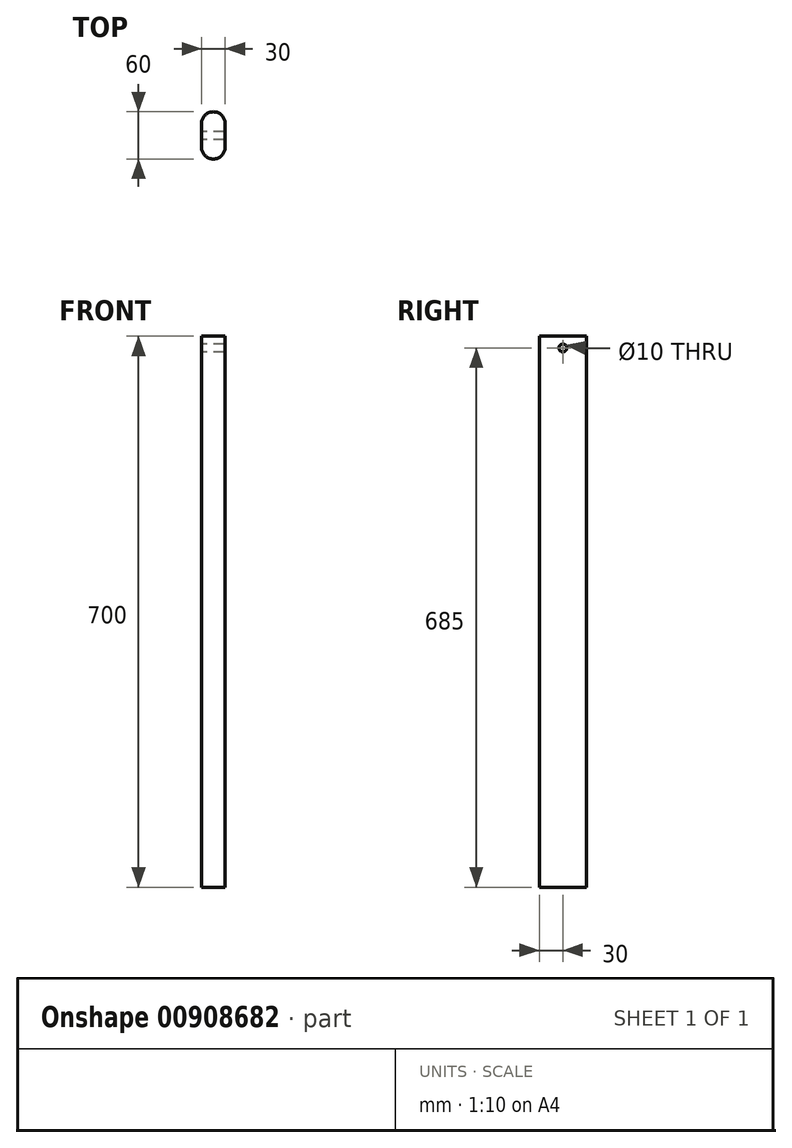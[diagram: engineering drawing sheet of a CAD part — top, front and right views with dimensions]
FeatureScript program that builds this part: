
annotation { "Feature Type Name" : "Feature", "Feature Type Description" : "" }
export const myFeature = defineFeature(function(context is Context, id is Id, definition is map)
    precondition{}
    {
        {
            var Q0;
            Q0=qCreatedBy(makeId("Top.planeOp"),FACE);
            var sketch = newSketch(context, id + "F0", { "sketchPlane" : qUnion([Q0])});
            skLineSegment(sketch, "E0.bottom", {"start": v(0, 30) * mm, "end": v(0, 30) * mm});
            skLineSegment(sketch, "E0.top", {"start": v(0, -30) * mm, "end": v(0, -30) * mm});
            skLineSegment(sketch, "E0.left", {"start": v(-15, 15) * mm, "end": v(-15, -15) * mm});
            skLineSegment(sketch, "E0.right", {"start": v(15, 15) * mm, "end": v(15, -15) * mm});
            skPoint(sketch, "E0.middle", {"position": v(0, 0) * mm});
            skPoint(sketch, "E1.visualSharp", {"position": v(-15, 30) * mm});
            skArc(sketch, "E1.filletArc", {"start": v(0, 30) * mm, "mid": v(-10.6, 25.6) * mm, "end": v(-15, 15) * mm});
            skPoint(sketch, "E2.visualSharp", {"position": v(-15, -30) * mm});
            skArc(sketch, "E2.filletArc", {"start": v(-15, -15) * mm, "mid": v(-10.6, -25.6) * mm, "end": v(0, -30) * mm});
            skPoint(sketch, "E3.visualSharp", {"position": v(15, -30) * mm});
            skArc(sketch, "E3.filletArc", {"start": v(0, -30) * mm, "mid": v(10.6, -25.6) * mm, "end": v(15, -15) * mm});
            skPoint(sketch, "E4.visualSharp", {"position": v(15, 30) * mm});
            skArc(sketch, "E4.filletArc", {"start": v(15, 15) * mm, "mid": v(10.6, 25.6) * mm, "end": v(0, 30) * mm});
            skSolve(sketch);
        }
        {
            var Q0;
            Q0=makeQuery(id+"F0.imprint","IMPRINT",FACE,{"disambiguationData":[TD([[makeQuery(id+"F0.imprint","IMPRINT",EDGE,{"derivedFrom":sQuery(id+"F0.wireOp",EDGE,"E0.left")}),1.0]])]});
            extrude(context, id + "F1", {"entities" : qUnion([Q0]), "oppositeDirection" : true, "depth" : 700 * mm, "offsetDistance" : 25 * mm});
        }
        {
            var Q0;
            Q0=makeQuery(id+"F1.opExtrude","SWEPT_FACE",FACE,{"disambiguationData":[OSD([sQuery(id+"F0.wireOp",EDGE,"E0.left")])]});
            var sketch = newSketch(context, id + "F2", { "sketchPlane" : qUnion([Q0])});
            skLineSegment(sketch, "E5.0", {"start": v(-15, -700) * mm, "end": v(-15, 0) * mm, "construction": true});
            skLineSegment(sketch, "E6", {"start": v(-15, 0) * mm, "end": v(0, 0) * mm, "construction": true});
            skLineSegment(sketch, "E7", {"start": v(0, 0) * mm, "end": v(0, -15) * mm, "construction": true});
            skCircle(sketch, "E8", {"center": v(0, -15) * mm, "radius": 5 * mm});
            skSolve(sketch);
        }
        {
            var Q0;
            Q0 = qSketchRegion(id + "F2", true);
            extrude(context, id + "F3", {"entities" : qUnion([Q0]), "operationType" : NewBodyOperationType.REMOVE, "oppositeDirection" : true, "depth" : 35 * mm, "offsetDistance" : 25 * mm});
        }
    });
